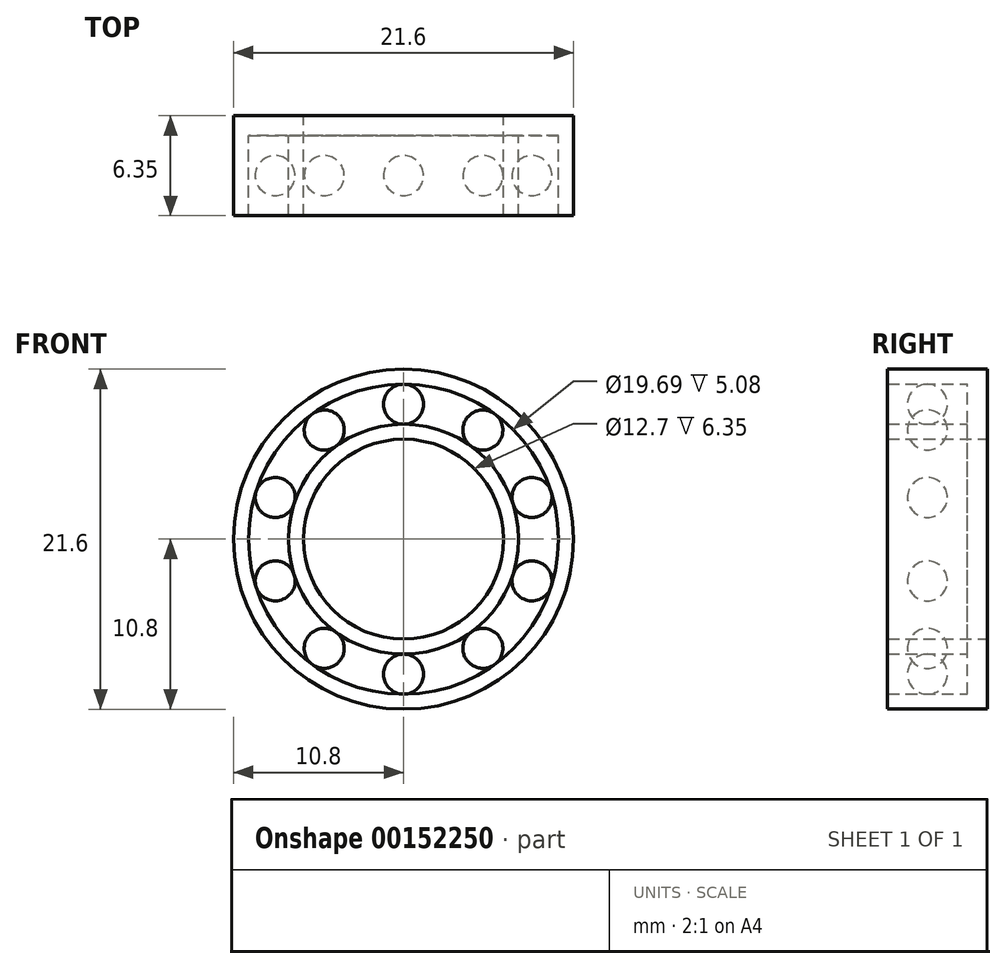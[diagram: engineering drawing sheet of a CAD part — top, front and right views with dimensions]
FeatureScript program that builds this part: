
annotation { "Feature Type Name" : "Feature", "Feature Type Description" : "" }
export const myFeature = defineFeature(function(context is Context, id is Id, definition is map)
    precondition{}
    {
        {
            var Q0;
            Q0=qCreatedBy(makeId("Front.planeOp"),FACE);
            var sketch = newSketch(context, id + "F0", { "sketchPlane" : qUnion([Q0])});
            skCircle(sketch, "E0", {"center": v(0, 0) * mm, "radius": 10.8 * mm});
            skCircle(sketch, "E1", {"center": v(0, 0) * mm, "radius": 6.35 * mm});
            skCircle(sketch, "E2", {"center": v(0, 0) * mm, "radius": 7.3 * mm});
            skCircle(sketch, "E3", {"center": v(0, 0) * mm, "radius": 9.84 * mm});
            skSolve(sketch);
        }
        {
            var Q0;
            Q0=makeQuery(id+"F0.imprint","IMPRINT",FACE,{"disambiguationData":[TD([[makeQuery(id+"F0.imprint","IMPRINT",EDGE,{"derivedFrom":sQuery(id+"F0.wireOp",EDGE,"E1")}),-1.0]])]});
            var Q1;
            Q1=makeQuery(id+"F0.imprint","IMPRINT",FACE,{"disambiguationData":[TD([[makeQuery(id+"F0.imprint","IMPRINT",EDGE,{"derivedFrom":sQuery(id+"F0.wireOp",EDGE,"E0")}),1.0]])]});
            extrude(context, id + "F1", {"entities" : qUnion([Q0, Q1]), "depth" : 6.35 * mm});
        }
        {
            var Q0;
            Q0=qCreatedBy(makeId("Front.planeOp"),FACE);
            var sketch = newSketch(context, id + "F2", { "sketchPlane" : qUnion([Q0])});
            skCircle(sketch, "E4.0", {"center": v(0, 0) * mm, "radius": 9.84 * mm});
            skSolve(sketch);
        }
        {
            var Q0;
            Q0=makeQuery(id+"F2.imprint","IMPRINT",FACE,{"disambiguationData":[TD([[makeQuery(id+"F2.imprint","IMPRINT",EDGE,{"derivedFrom":sQuery(id+"F2.wireOp",EDGE,"E4.0")}),1.0]])]});
            extrude(context, id + "F3", {"entities" : qUnion([Q0]), "operationType" : NewBodyOperationType.ADD, "depth" : 1.27 * mm});
        }
        {
            var Q0;
            Q0=qCreatedBy(makeId("Right.planeOp"),FACE);
            var sketch = newSketch(context, id + "F4", { "sketchPlane" : qUnion([Q0])});
            skLineSegment(sketch, "E5.0", {"start": v(-1.27, -9.84) * mm, "end": v(-1.27, 9.84) * mm});
            skLineSegment(sketch, "E6.0", {"start": v(-6.35, -7.3) * mm, "end": v(-6.35, 7.3) * mm});
            skLineSegment(sketch, "E7.0", {"start": v(-6.35, -10.8) * mm, "end": v(-6.35, 10.8) * mm});
            skLineSegment(sketch, "E8", {"start": v(-3.81, -9.24) * mm, "end": v(-3.81, 8.24) * mm});
            skSolve(sketch);
        }
        {
            var Q0;
            Q0=sQuery(id+"F4.wireOp",EDGE,"E8");
            var Q1;
            Q1=qCreatedBy(makeId("Front.planeOp"),FACE);
            cPlane(context, id + "F5", {"entities" : qUnion([Q0, Q1]), "cplaneType" : CPlaneType.LINE_ANGLE, "offset" : 25.4 * mm, "angle" : 0 * degree, "width" : 152.4 * mm, "height" : 152.4 * mm});
        }
        {
            var Q0;
            Q0=qCreatedBy(id+"F5.planeOp",FACE);
            var sketch = newSketch(context, id + "F6", { "sketchPlane" : qUnion([Q0])});
            skCircle(sketch, "E9.0", {"center": v(0, 0) * mm, "radius": 7.3 * mm, "construction": true});
            skCircle(sketch, "E10.0", {"center": v(0, 0) * mm, "radius": 9.84 * mm, "construction": true});
            skCircle(sketch, "E11", {"center": v(0, 0) * mm, "radius": 8.57 * mm, "construction": true});
            skCircle(sketch, "E12", {"center": v(0, 8.57) * mm, "radius": 1.27 * mm});
            skCircle(sketch, "E13.1.0", {"center": v(-5.04, 6.94) * mm, "radius": 1.27 * mm});
            skCircle(sketch, "E13.2.0", {"center": v(-8.15, 2.65) * mm, "radius": 1.27 * mm});
            skCircle(sketch, "E13.3.0", {"center": v(-8.15, -2.65) * mm, "radius": 1.27 * mm});
            skCircle(sketch, "E13.4.0", {"center": v(-5.04, -6.94) * mm, "radius": 1.27 * mm});
            skCircle(sketch, "E13.5.0", {"center": v(0, -8.57) * mm, "radius": 1.27 * mm});
            skCircle(sketch, "E13.6.0", {"center": v(5.04, -6.94) * mm, "radius": 1.27 * mm});
            skCircle(sketch, "E13.7.0", {"center": v(8.15, -2.65) * mm, "radius": 1.27 * mm});
            skCircle(sketch, "E13.8.0", {"center": v(8.15, 2.65) * mm, "radius": 1.27 * mm});
            skCircle(sketch, "E13.9.0", {"center": v(5.04, 6.94) * mm, "radius": 1.27 * mm});
            skLineSegment(sketch, "E14", {"start": v(0, -9.84) * mm, "end": v(0, 9.84) * mm});
            skLineSegment(sketch, "E15", {"start": v(9.36, -3.04) * mm, "end": v(-9.36, 3.04) * mm});
            skLineSegment(sketch, "E16", {"start": v(5.79, 7.96) * mm, "end": v(-5.79, -7.96) * mm});
            skLineSegment(sketch, "E17", {"start": v(5.79, -7.96) * mm, "end": v(-5.79, 7.96) * mm});
            skLineSegment(sketch, "E18", {"start": v(9.36, 3.04) * mm, "end": v(-9.36, -3.04) * mm});
            skSolve(sketch);
        }
        {
            var Q0;
            {var subQ0=sQuery(id+"F6.wireOp",EDGE,"E14");var subQ1=sQuery(id+"F6.wireOp",EDGE,"E12");var subQ2=makeQuery(id+"F6.imprint","INTERSECT",VERTEX,{"disambiguationData":[OD(0.0)],"derivedFrom":[subQ1,subQ0]});Q0=makeQuery(id+"F6.imprint","IMPRINT",FACE,{"disambiguationData":[TD([[makeQuery(id+"F6.imprint","IMPRINT",EDGE,{"disambiguationData":[TD([[subQ2,1.0]])],"derivedFrom":subQ1}),1.0]])]});}
            var Q1;
            {var subQ0=sQuery(id+"F6.wireOp",EDGE,"E14");var subQ1=sQuery(id+"F6.wireOp",EDGE,"E13.5.0");var subQ2=makeQuery(id+"F6.imprint","INTERSECT",VERTEX,{"disambiguationData":[OD(0.0)],"derivedFrom":[subQ1,subQ0]});Q1=makeQuery(id+"F6.imprint","IMPRINT",FACE,{"disambiguationData":[TD([[makeQuery(id+"F6.imprint","IMPRINT",EDGE,{"disambiguationData":[TD([[subQ2,1.0]])],"derivedFrom":subQ1}),1.0]])]});}
            var Q2;
            Q2=sQuery(id+"F6.wireOp",EDGE,"E14");
            revolve(context, id + "F7", {"operationType" : NewBodyOperationType.ADD, "entities" : qUnion([Q0, Q1]), "axis" : qUnion([Q2]), "revolveType" : RevolveType.FULL});
        }
        {
            var Q0;
            {var subQ0=sQuery(id+"F6.wireOp",EDGE,"E16");var subQ1=sQuery(id+"F6.wireOp",EDGE,"E13.9.0");var subQ2=makeQuery(id+"F6.imprint","INTERSECT",VERTEX,{"disambiguationData":[OD(0.0)],"derivedFrom":[subQ1,subQ0]});Q0=makeQuery(id+"F6.imprint","IMPRINT",FACE,{"disambiguationData":[TD([[makeQuery(id+"F6.imprint","IMPRINT",EDGE,{"disambiguationData":[TD([[subQ2,-1.0]])],"derivedFrom":subQ1}),1.0]])]});}
            var Q1;
            {var subQ0=sQuery(id+"F6.wireOp",EDGE,"E16");var subQ1=sQuery(id+"F6.wireOp",EDGE,"E13.4.0");var subQ2=makeQuery(id+"F6.imprint","INTERSECT",VERTEX,{"disambiguationData":[OD(0.0)],"derivedFrom":[subQ1,subQ0]});Q1=makeQuery(id+"F6.imprint","IMPRINT",FACE,{"disambiguationData":[TD([[makeQuery(id+"F6.imprint","IMPRINT",EDGE,{"disambiguationData":[TD([[subQ2,1.0]])],"derivedFrom":subQ1}),1.0]])]});}
            var Q2;
            Q2=sQuery(id+"F6.wireOp",EDGE,"E16");
            revolve(context, id + "F8", {"entities" : qUnion([Q0, Q1]), "axis" : qUnion([Q2]), "revolveType" : RevolveType.FULL});
        }
        {
            var Q0;
            {var subQ0=sQuery(id+"F6.wireOp",EDGE,"E17");var subQ1=sQuery(id+"F6.wireOp",EDGE,"E13.1.0");var subQ2=makeQuery(id+"F6.imprint","INTERSECT",VERTEX,{"disambiguationData":[OD(0.0)],"derivedFrom":[subQ1,subQ0]});Q0=makeQuery(id+"F6.imprint","IMPRINT",FACE,{"disambiguationData":[TD([[makeQuery(id+"F6.imprint","IMPRINT",EDGE,{"disambiguationData":[TD([[subQ2,1.0]])],"derivedFrom":subQ1}),1.0]])]});}
            var Q1;
            {var subQ0=sQuery(id+"F6.wireOp",EDGE,"E17");var subQ1=sQuery(id+"F6.wireOp",EDGE,"E13.6.0");var subQ2=makeQuery(id+"F6.imprint","INTERSECT",VERTEX,{"disambiguationData":[OD(0.0)],"derivedFrom":[subQ1,subQ0]});Q1=makeQuery(id+"F6.imprint","IMPRINT",FACE,{"disambiguationData":[TD([[makeQuery(id+"F6.imprint","IMPRINT",EDGE,{"disambiguationData":[TD([[subQ2,-1.0]])],"derivedFrom":subQ1}),1.0]])]});}
            var Q2;
            Q2=sQuery(id+"F6.wireOp",EDGE,"E17");
            revolve(context, id + "F9", {"entities" : qUnion([Q0, Q1]), "axis" : qUnion([Q2]), "revolveType" : RevolveType.FULL});
        }
        {
            var Q0;
            {var subQ0=sQuery(id+"F6.wireOp",EDGE,"E18");var subQ1=sQuery(id+"F6.wireOp",EDGE,"E13.8.0");var subQ2=makeQuery(id+"F6.imprint","INTERSECT",VERTEX,{"disambiguationData":[OD(0.0)],"derivedFrom":[subQ1,subQ0]});Q0=makeQuery(id+"F6.imprint","IMPRINT",FACE,{"disambiguationData":[TD([[makeQuery(id+"F6.imprint","IMPRINT",EDGE,{"disambiguationData":[TD([[subQ2,-1.0]])],"derivedFrom":subQ1}),1.0]])]});}
            var Q1;
            {var subQ0=sQuery(id+"F6.wireOp",EDGE,"E18");var subQ1=sQuery(id+"F6.wireOp",EDGE,"E13.3.0");var subQ2=makeQuery(id+"F6.imprint","INTERSECT",VERTEX,{"disambiguationData":[OD(0.0)],"derivedFrom":[subQ1,subQ0]});Q1=makeQuery(id+"F6.imprint","IMPRINT",FACE,{"disambiguationData":[TD([[makeQuery(id+"F6.imprint","IMPRINT",EDGE,{"disambiguationData":[TD([[subQ2,1.0]])],"derivedFrom":subQ1}),1.0]])]});}
            var Q2;
            Q2=sQuery(id+"F6.wireOp",EDGE,"E18");
            revolve(context, id + "F10", {"entities" : qUnion([Q0, Q1]), "axis" : qUnion([Q2]), "revolveType" : RevolveType.FULL});
        }
        {
            var Q0;
            {var subQ0=sQuery(id+"F6.wireOp",EDGE,"E15");var subQ1=sQuery(id+"F6.wireOp",EDGE,"E13.7.0");var subQ2=makeQuery(id+"F6.imprint","INTERSECT",VERTEX,{"disambiguationData":[OD(0.0)],"derivedFrom":[subQ1,subQ0]});Q0=makeQuery(id+"F6.imprint","IMPRINT",FACE,{"disambiguationData":[TD([[makeQuery(id+"F6.imprint","IMPRINT",EDGE,{"disambiguationData":[TD([[subQ2,-1.0]])],"derivedFrom":subQ1}),1.0]])]});}
            var Q1;
            {var subQ0=sQuery(id+"F6.wireOp",EDGE,"E15");var subQ1=sQuery(id+"F6.wireOp",EDGE,"E13.2.0");var subQ2=makeQuery(id+"F6.imprint","INTERSECT",VERTEX,{"disambiguationData":[OD(0.0)],"derivedFrom":[subQ1,subQ0]});Q1=makeQuery(id+"F6.imprint","IMPRINT",FACE,{"disambiguationData":[TD([[makeQuery(id+"F6.imprint","IMPRINT",EDGE,{"disambiguationData":[TD([[subQ2,1.0]])],"derivedFrom":subQ1}),1.0]])]});}
            var Q2;
            Q2=sQuery(id+"F6.wireOp",EDGE,"E15");
            revolve(context, id + "F11", {"entities" : qUnion([Q0, Q1]), "axis" : qUnion([Q2]), "revolveType" : RevolveType.FULL});
        }
        {
            var Q0;
            Q0=qCreatedBy(id+"F5.planeOp",FACE);
            var sketch = newSketch(context, id + "F12", { "sketchPlane" : qUnion([Q0])});
            skCircle(sketch, "E19", {"center": v(0, 0) * mm, "radius": 6.35 * mm});
            skSolve(sketch);
        }
        {
            var Q0;
            Q0=makeQuery(id+"F12.imprint","IMPRINT",FACE,{"disambiguationData":[TD([[makeQuery(id+"F12.imprint","IMPRINT",EDGE,{"derivedFrom":sQuery(id+"F12.wireOp",EDGE,"E19")}),1.0]])]});
            extrude(context, id + "F13", {"entities" : qUnion([Q0]), "operationType" : NewBodyOperationType.REMOVE, "depth" : 25.4 * mm});
        }
    });
